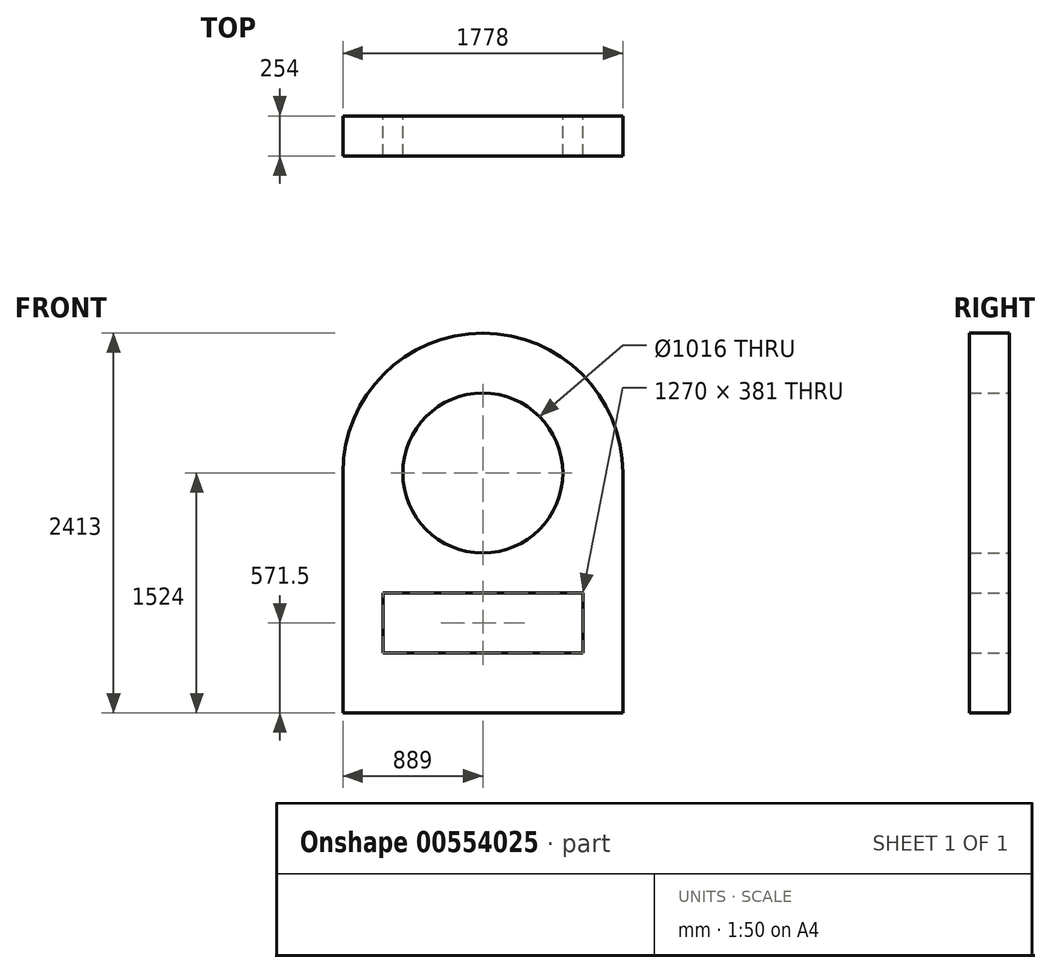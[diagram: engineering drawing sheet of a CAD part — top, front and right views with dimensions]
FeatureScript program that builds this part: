
annotation { "Feature Type Name" : "Feature", "Feature Type Description" : "" }
export const myFeature = defineFeature(function(context is Context, id is Id, definition is map)
    precondition{}
    {
        {
            var Q0;
            Q0=qCreatedBy(makeId("Front.planeOp"),FACE);
            var sketch = newSketch(context, id + "F0", { "sketchPlane" : qUnion([Q0])});
            skLineSegment(sketch, "E0", {"start": v(0, 0) * mm, "end": v(1778, 0) * mm});
            skLineSegment(sketch, "E1", {"start": v(0, 0) * mm, "end": v(0, 1524) * mm});
            skLineSegment(sketch, "E2", {"start": v(1778, 0) * mm, "end": v(1778, 1524) * mm});
            skCircle(sketch, "E3", {"center": v(889, 1524) * mm, "radius": 508 * mm});
            skArc(sketch, "E4", {"start": v(1778, 1524) * mm, "mid": v(889, 2413) * mm, "end": v(0, 1524) * mm});
            skLineSegment(sketch, "E5", {"start": v(254, 762) * mm, "end": v(254, 381) * mm});
            skLineSegment(sketch, "E6", {"start": v(254, 762) * mm, "end": v(1524, 762) * mm});
            skLineSegment(sketch, "E7", {"start": v(1524, 762) * mm, "end": v(1524, 381) * mm});
            skLineSegment(sketch, "E8", {"start": v(1524, 381) * mm, "end": v(254, 381) * mm});
            skSolve(sketch);
        }
        {
            var Q0;
            Q0=makeQuery(id+"F0.imprint","IMPRINT",FACE,{"disambiguationData":[TD([[makeQuery(id+"F0.imprint","IMPRINT",EDGE,{"derivedFrom":sQuery(id+"F0.wireOp",EDGE,"E0")}),1.0]])]});
            extrude(context, id + "F1", {"entities" : qUnion([Q0]), "depth" : 254 * mm, "offsetDistance" : 25.4 * mm});
        }
    });
